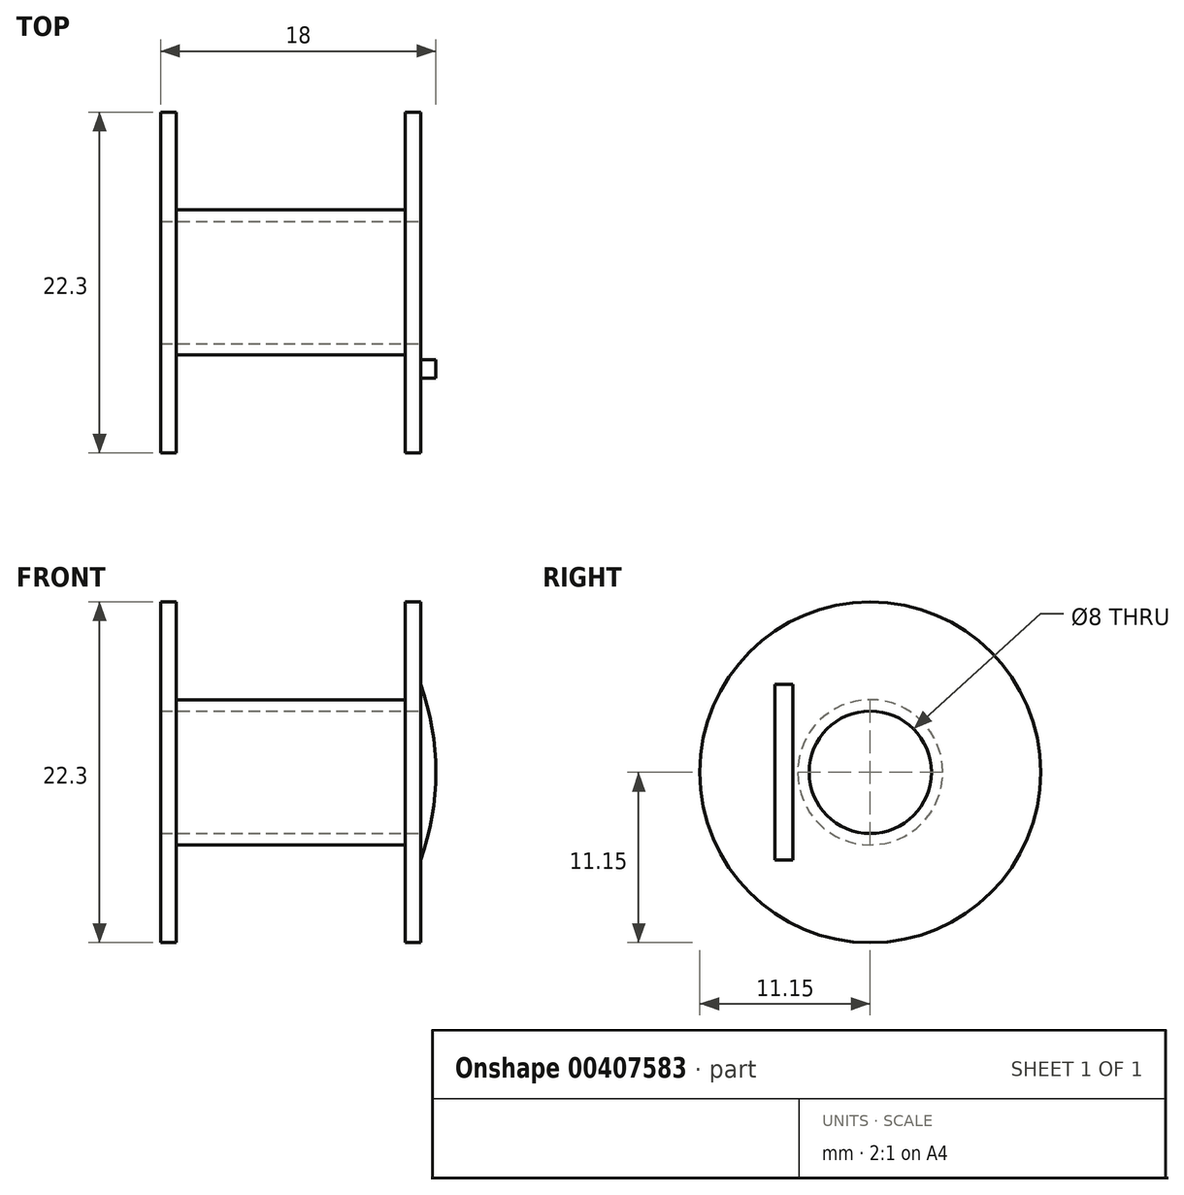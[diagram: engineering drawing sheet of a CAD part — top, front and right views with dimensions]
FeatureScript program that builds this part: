
annotation { "Feature Type Name" : "Feature", "Feature Type Description" : "" }
export const myFeature = defineFeature(function(context is Context, id is Id, definition is map)
    precondition{}
    {
        {
            var Q0;
            Q0=qCreatedBy(makeId("Front.planeOp"),FACE);
            var sketch = newSketch(context, id + "F0", { "sketchPlane" : qUnion([Q0])});
            skLineSegment(sketch, "E0", {"start": v(0, 4) * mm, "end": v(17, 4) * mm});
            skLineSegment(sketch, "E1", {"start": v(17, 4) * mm, "end": v(17, 11.15) * mm});
            skLineSegment(sketch, "E2", {"start": v(17, 11.15) * mm, "end": v(16, 11.15) * mm});
            skLineSegment(sketch, "E3", {"start": v(16, 11.15) * mm, "end": v(16, 4.75) * mm});
            skLineSegment(sketch, "E4", {"start": v(16, 4.75) * mm, "end": v(1, 4.75) * mm});
            skLineSegment(sketch, "E5", {"start": v(1, 4.75) * mm, "end": v(1, 11.15) * mm});
            skLineSegment(sketch, "E6", {"start": v(1, 11.15) * mm, "end": v(0, 11.15) * mm});
            skLineSegment(sketch, "E7", {"start": v(0, 11.15) * mm, "end": v(0, 4) * mm});
            skLineSegment(sketch, "E8", {"start": v(19.72, 0) * mm, "end": v(0, 0) * mm, "construction": true});
            skSolve(sketch);
        }
        {
            var Q0;
            Q0=makeQuery(id+"F0.imprint","IMPRINT",FACE,{"disambiguationData":[TD([[makeQuery(id+"F0.imprint","IMPRINT",EDGE,{"derivedFrom":sQuery(id+"F0.wireOp",EDGE,"E0")}),1.0]])]});
            var Q1;
            Q1=sQuery(id+"F0.wireOp",EDGE,"E8");
            revolve(context, id + "F1", {"entities" : qUnion([Q0]), "axis" : qUnion([Q1]), "revolveType" : RevolveType.FULL});
        }
        {
            var Q0;
            Q0=qCreatedBy(makeId("Front.planeOp"),FACE);
            var sketch = newSketch(context, id + "F2", { "sketchPlane" : qUnion([Q0])});
            skArc(sketch, "E9", {"start": v(17, -5.75) * mm, "mid": v(18, 0) * mm, "end": v(17, 5.75) * mm});
            skLineSegment(sketch, "E10", {"start": v(17, 5.75) * mm, "end": v(17, -5.75) * mm});
            skSolve(sketch);
        }
        {
            var Q0;
            Q0=makeQuery(id+"F2.imprint","IMPRINT",FACE,{"disambiguationData":[TD([[makeQuery(id+"F2.imprint","IMPRINT",EDGE,{"derivedFrom":sQuery(id+"F2.wireOp",EDGE,"E9")}),1.0]])]});
            extrude(context, id + "F3", {"entities" : qUnion([Q0]), "operationType" : NewBodyOperationType.ADD, "depth" : 6.25 * mm, "hasSecondDirection" : true, "secondDirectionOppositeDirection" : false, "secondDirectionDepth" : 5.05 * mm});
        }
    });
